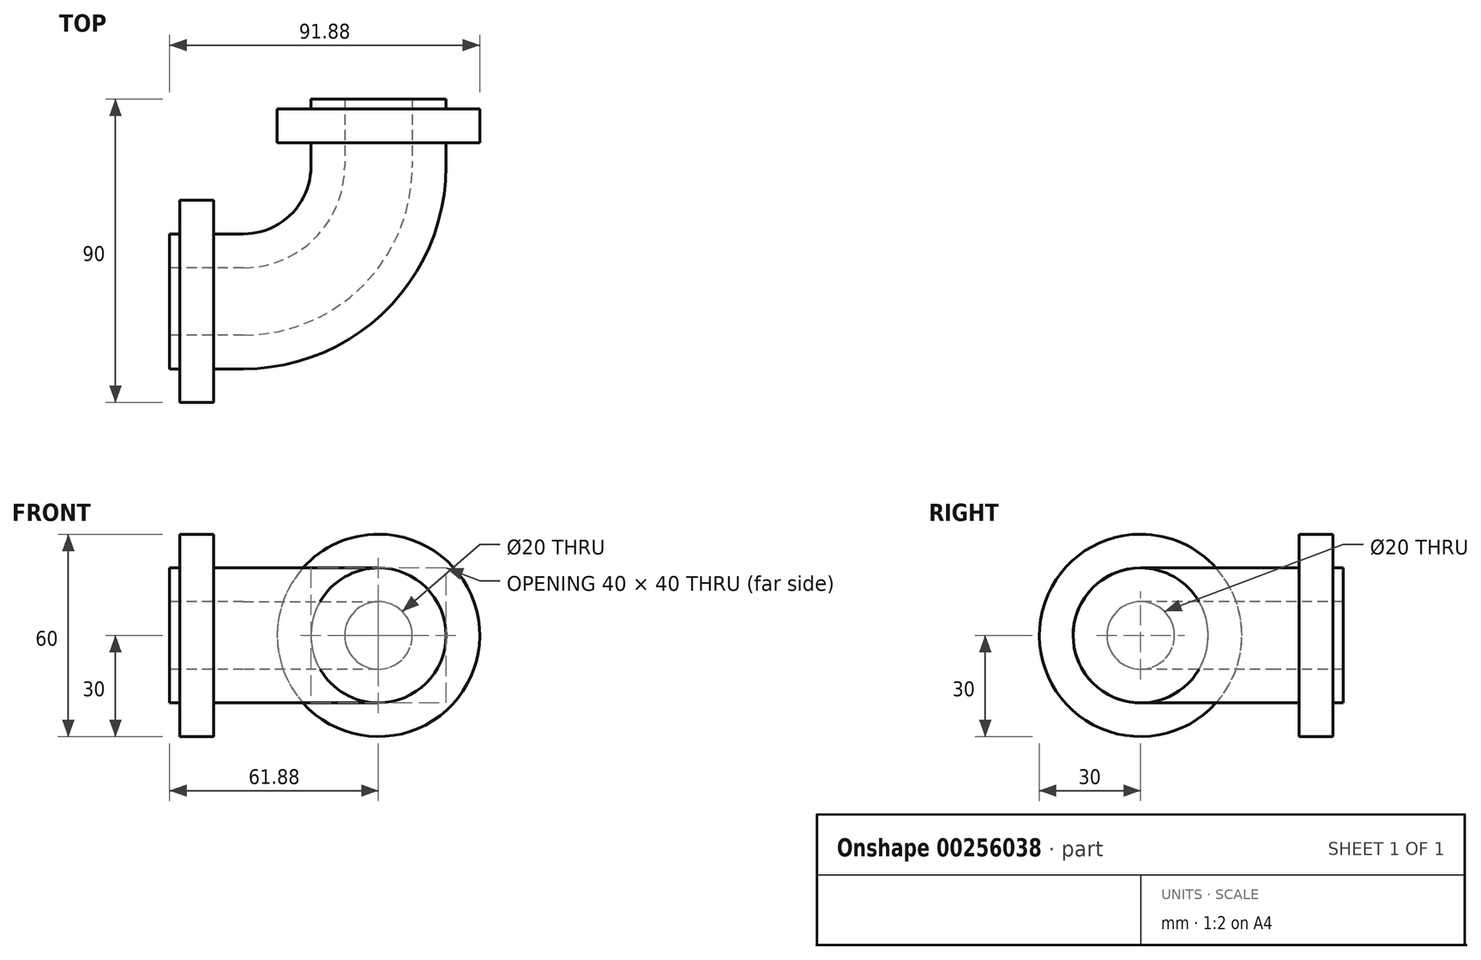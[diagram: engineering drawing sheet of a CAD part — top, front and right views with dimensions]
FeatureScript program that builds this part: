
annotation { "Feature Type Name" : "Feature", "Feature Type Description" : "" }
export const myFeature = defineFeature(function(context is Context, id is Id, definition is map)
    precondition{}
    {
        {
            var Q0;
            Q0=qCreatedBy(makeId("Front.planeOp"),FACE);
            var sketch = newSketch(context, id + "F0", { "sketchPlane" : qUnion([Q0])});
            skCircle(sketch, "E0", {"center": v(0, 0) * mm, "radius": 10 * mm});
            skCircle(sketch, "E1", {"center": v(0, 0) * mm, "radius": 20 * mm});
            skSolve(sketch);
        }
        {
            var Q0;
            Q0=qCreatedBy(makeId("Top.planeOp"),FACE);
            var sketch = newSketch(context, id + "F1", { "sketchPlane" : qUnion([Q0])});
            skLineSegment(sketch, "E2", {"start": v(0, 0) * mm, "end": v(0, -20) * mm});
            skArc(sketch, "E3", {"start": v(0, -20) * mm, "mid": v(-11.72, -48.28) * mm, "end": v(-40, -60) * mm});
            skLineSegment(sketch, "E4", {"start": v(-40, -60) * mm, "end": v(-61.88, -60) * mm});
            skLineSegment(sketch, "E5.0.0", {"start": v(20, 0) * mm, "end": v(-20, 0) * mm});
            skSolve(sketch);
        }
        {
            var Q0;
            Q0=makeQuery(id+"F0.imprint","IMPRINT",FACE,{"disambiguationData":[TD([[makeQuery(id+"F0.imprint","IMPRINT",EDGE,{"derivedFrom":sQuery(id+"F0.wireOp",EDGE,"E0")}),-1.0]])]});
            var Q1;
            Q1=sQuery(id+"F1.wireOp",EDGE,"E2");
            var Q2;
            Q2=sQuery(id+"F1.wireOp",EDGE,"E3");
            var Q3;
            Q3=sQuery(id+"F1.wireOp",EDGE,"E4");
            sweep(context, id + "F2", {"profiles" : qUnion([Q0]), "path" : qUnion([Q1, Q2, Q3])});
        }
        {
            var Q0;
            Q0=makeQuery(id+"F2.opSweep","CAP_FACE",FACE,{"disambiguationData":[OSD([sQuery(id+"F0.wireOp",EDGE,"E0"),sQuery(id+"F0.wireOp",EDGE,"E1"),sQuery(id+"F1.wireOp",VERTEX,"E4.end")])],"isStart":false});
            cPlane(context, id + "F3", {"entities" : qUnion([Q0]), "cplaneType" : CPlaneType.OFFSET, "offset" : 3 * mm, "oppositeDirection" : true, "width" : 150 * mm, "height" : 150 * mm});
        }
        {
            var Q0;
            Q0=qCreatedBy(id+"F3.planeOp",FACE);
            var sketch = newSketch(context, id + "F4", { "sketchPlane" : qUnion([Q0])});
            skCircle(sketch, "E6.0.0", {"center": v(60, 0) * mm, "radius": 20 * mm});
            skCircle(sketch, "E7", {"center": v(60, 0) * mm, "radius": 30 * mm});
            skSolve(sketch);
        }
        {
            var Q0;
            Q0=makeQuery(id+"F4.imprint","IMPRINT",FACE,{"disambiguationData":[TD([[makeQuery(id+"F4.imprint","IMPRINT",EDGE,{"derivedFrom":sQuery(id+"F4.wireOp",EDGE,"E6.0.0")}),-1.0]])]});
            extrude(context, id + "F5", {"entities" : qUnion([Q0]), "operationType" : NewBodyOperationType.ADD, "oppositeDirection" : true, "depth" : 10 * mm});
        }
        {
            var Q0;
            Q0=makeQuery(id+"F2.opSweep","CAP_FACE",FACE,{"disambiguationData":[OSD([sQuery(id+"F0.wireOp",EDGE,"E0"),sQuery(id+"F0.wireOp",EDGE,"E1"),sQuery(id+"F1.wireOp",VERTEX,"E2.start")])],"isStart":true});
            cPlane(context, id + "F6", {"entities" : qUnion([Q0]), "cplaneType" : CPlaneType.OFFSET, "offset" : 3 * mm, "oppositeDirection" : true, "width" : 150 * mm, "height" : 150 * mm});
        }
        {
            var Q0;
            Q0=qCreatedBy(id+"F6.planeOp",FACE);
            var sketch = newSketch(context, id + "F7", { "sketchPlane" : qUnion([Q0])});
            skCircle(sketch, "E8.0.0", {"center": v(0, 0) * mm, "radius": 20 * mm});
            skCircle(sketch, "E9", {"center": v(0, 0) * mm, "radius": 30 * mm});
            skSolve(sketch);
        }
        {
            var Q0;
            Q0 = qSketchRegion(id + "F7", true);
            extrude(context, id + "F8", {"entities" : qUnion([Q0]), "operationType" : NewBodyOperationType.ADD, "oppositeDirection" : true, "depth" : 10 * mm});
        }
    });
